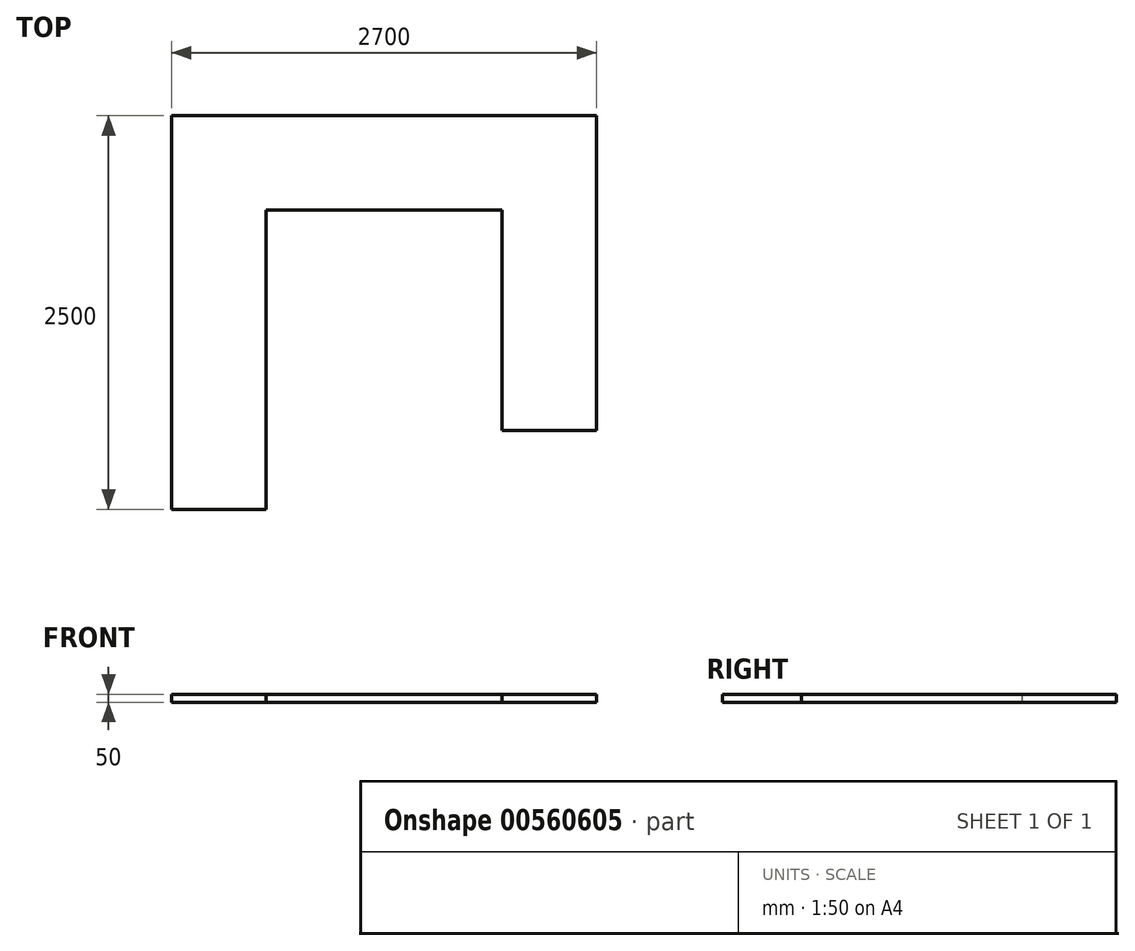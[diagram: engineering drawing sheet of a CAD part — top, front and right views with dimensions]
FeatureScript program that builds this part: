
annotation { "Feature Type Name" : "Feature", "Feature Type Description" : "" }
export const myFeature = defineFeature(function(context is Context, id is Id, definition is map)
    precondition{}
    {
        {
            var Q0;
            Q0=qCreatedBy(makeId("Top.planeOp"),FACE);
            var sketch = newSketch(context, id + "F0", { "sketchPlane" : qUnion([Q0])});
            skLineSegment(sketch, "E0.top", {"start": v(0, -2500) * mm, "end": v(600, -2500) * mm});
            skLineSegment(sketch, "E0.left", {"start": v(0, 0) * mm, "end": v(0, -2500) * mm});
            skLineSegment(sketch, "E0.right", {"start": v(600, -600) * mm, "end": v(600, -2500) * mm});
            skLineSegment(sketch, "E1.top", {"start": v(600, -600) * mm, "end": v(2100, -600) * mm});
            skLineSegment(sketch, "E2.top", {"start": v(2700, -2000) * mm, "end": v(2100, -2000) * mm});
            skLineSegment(sketch, "E2.right", {"start": v(2100, -600) * mm, "end": v(2100, -2000) * mm});
            skLineSegment(sketch, "E3", {"start": v(2700, 0) * mm, "end": v(2700, -2000) * mm});
            skLineSegment(sketch, "E4", {"start": v(0, 0) * mm, "end": v(2700, 0) * mm});
            skSolve(sketch);
        }
        {
            var Q0;
            Q0 = qSketchRegion(id + "F0", true);
            extrude(context, id + "F1", {"entities" : qUnion([Q0]), "depth" : 50 * mm, "offsetDistance" : 25 * mm});
        }
    });
